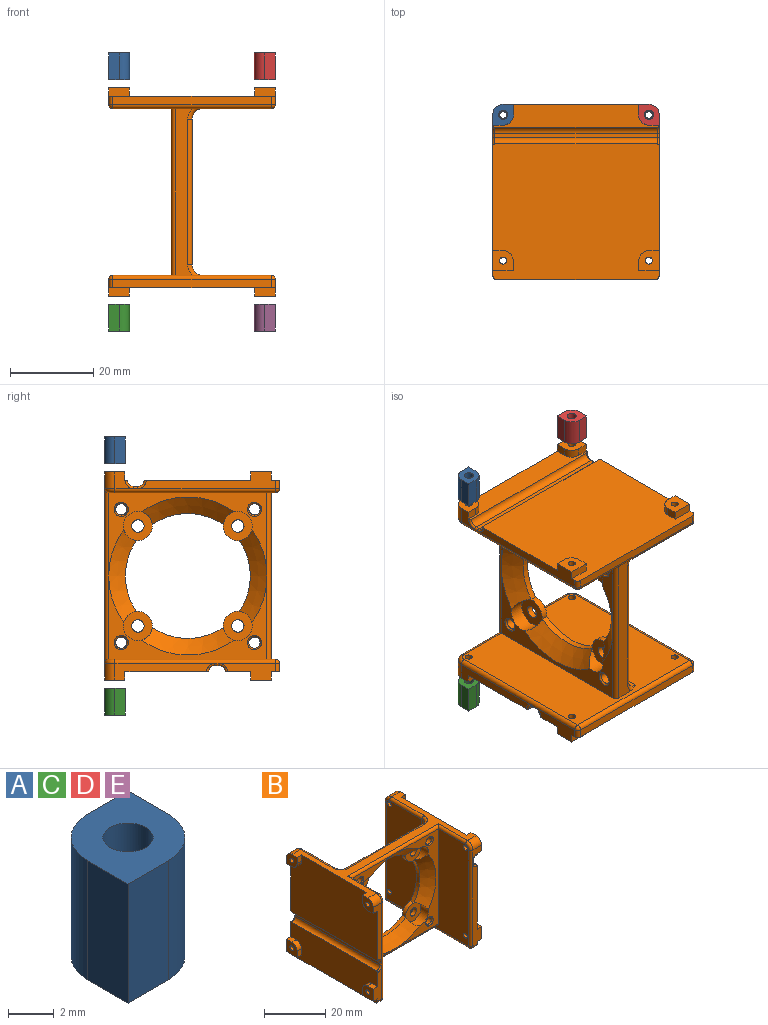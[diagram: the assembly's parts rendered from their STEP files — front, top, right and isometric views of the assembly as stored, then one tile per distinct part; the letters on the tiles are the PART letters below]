
ASSEMBLY  parts=5 mates=4
PART A: 9 faces, bbox 5x5x6.4 mm
  f0: plane 6.4x2.5mm, normal (1,0,0), area 16mm2, adj f1,f5,f6,f7
  f1: plane 6.4x2.5mm, normal (0,1,0), area 16mm2, adj f0,f2,f6,f7
  f2: cylinder r=2.5mm len=6.4mm, axis (0,0,-1), area 25.1mm2, adj f1,f3,f6,f7
  f3: plane 6.4x2.5mm, normal (-1,0,0), area 16mm2, adj f2,f4,f6,f7
  f4: plane 6.4x2.5mm, normal (0,-1,0), area 16mm2, adj f3,f5,f6,f7
  f5: cylinder r=2.5mm len=6.4mm, axis (0,0,-1), area 25.1mm2, adj f0,f4,f6,f7
  f6: plane 5x5mm, normal (0,0,1), area 18.5mm2, adj f0,f1,f2,f3,f4,f5,f8
  f7: plane 5x5mm, normal (0,0,-1), area 18.5mm2, adj f0,f1,f2,f3,f4,f5,f8
  f8: cylinder r=1.1mm len=6.4mm, axis (0,0,-1), area 44.2mm2, adj f6,f7
PART B: 151 faces, bbox 50x40.4x42.2 mm
  f0: plane 13.5x4mm, normal (0,-1,0), area 33.7mm2, adj f5,f10,f63,f66,f122,f126,f150
  f1: plane 13.5x4mm, normal (0,1,0), area 33.7mm2, adj f6,f10,f61,f62,f115,f116,f147
  f2: plane 33x4mm, normal (0,-1,0), area 72.7mm2, adj f8,f16,f78,f79,f117,f123,f144
  f3: plane 33x4mm, normal (0,1,0), area 72.7mm2, adj f7,f16,f80,f83,f111,f112,f141
  f4: plane 38x20mm, normal (0,-1,0), area 162.1mm2, adj f14,f19,f23,f29,f35,f41,f44,f50
  f5: plane 4.9x2mm, normal (0,0,-1), area 9.8mm2, adj f0,f10,f65,f66
  f6: plane 4.9x2mm, normal (0,0,-1), area 9.8mm2, adj f1,f10,f59,f62
  f7: plane 4.9x2mm, normal (0,0,-1), area 9.8mm2, adj f3,f16,f82,f83
  f8: plane 4.9x2mm, normal (0,0,-1), area 9.8mm2, adj f2,f16,f76,f79
  f9: plane 40x5.5mm, normal (1,0,0), area 174.3mm2, adj f12,f15,f26,f72,f73,f74,f85,f86
  f10: plane 40x13mm, normal (-1,0,0), area 473.9mm2, adj f0,f1,f5,f6,f59,f60,f61,f63
  f11: plane 24x4mm, normal (0,1,0), area 49.7mm2, adj f17,f56,f58,f97,f115,f145
  f12: plane 4.5x4mm, normal (0,1,0), area 10.7mm2, adj f9,f84,f87,f88,f112,f139
  f13: plane 40x38mm, normal (-1,0,0), area 1218.6mm2, adj f18,f28,f89,f90,f91,f92,f103,f107
  f14: plane 40x38mm, normal (1,0,0), area 1218.6mm2, adj f4,f28,f93,f94,f95,f96,f104,f110
  f15: plane 50x35mm, normal (0,0,1), area 290.5mm2, adj f9,f17,f55,f58,f67,f70,f71,f74
  f16: plane 40x32.5mm, normal (1,0,0), area 1253.9mm2, adj f2,f3,f7,f8,f76,f77,f78,f80
  f17: plane 40x25mm, normal (-1,0,0), area 954.3mm2, adj f11,f15,f25,f55,f56,f57,f67,f68
  f18: plane 38x20mm, normal (0,-1,0), area 162.1mm2, adj f13,f19,f21,f23,f37,f39,f46,f48
  f19: cone r=19mm half-angle=48.8deg, axis (0,-1,0), area 106.8mm2, adj f4,f18,f20,f35,f37
  f20: cylinder r=15mm len=17.03mm, axis (0,-1,0), area 27.2mm2, adj f19,f27,f33,f34
  f21: cone r=19mm half-angle=48.8deg, axis (0,-1,0), area 106.8mm2, adj f18,f22,f37,f39
  f22: cylinder r=15mm len=17.03mm, axis (0,-1,0), area 27.2mm2, adj f21,f27,f32,f33
  f23: cone r=19mm half-angle=48.8deg, axis (0,-1,0), area 106.8mm2, adj f4,f18,f24,f39,f41
  f24: cylinder r=15mm len=17.03mm, axis (0,-1,0), area 27.2mm2, adj f23,f27,f31,f32
  f25: plane 24x4mm, normal (0,-1,0), area 49.7mm2, adj f17,f69,f70,f98,f126,f148
  f26: plane 4.5x4mm, normal (0,-1,0), area 10.7mm2, adj f9,f71,f72,f75,f123,f142
  f27: plane 38x35mm, normal (0,1,0), area 594.9mm2, adj f20,f22,f24,f30,f31,f32,f33,f34
  f28: plane 40x4.05mm, normal (0,0,-1), area 121.6mm2, adj f13,f14,f131,f132,f133,f134
  f29: cone r=19mm half-angle=48.8deg, axis (0,-1,0), area 106.8mm2, adj f4,f30,f35,f41
  f30: cylinder r=15mm len=17.03mm, axis (0,-1,0), area 27.2mm2, adj f27,f29,f31,f34
  f31: cylinder r=3.5mm len=3.85mm, axis (0,-1,0), area 9.3mm2, adj f24,f27,f30,f42
  f32: cylinder r=3.5mm len=3.85mm, axis (0,-1,0), area 9.3mm2, adj f22,f24,f27,f40
  f33: cylinder r=3.5mm len=3.85mm, axis (0,-1,0), area 9.3mm2, adj f20,f22,f27,f38
  f34: cylinder r=3.5mm len=3.85mm, axis (0,-1,0), area 9.3mm2, adj f20,f27,f30,f36
  f35: cylinder r=3.5mm len=6.98mm, axis (0,-1,0), area 40.3mm2, adj f4,f19,f29,f36
  f36: plane 7x7mm, normal (0,-1,0), area 31.4mm2, adj f34,f35,f54
  f37: cylinder r=3.5mm len=6.98mm, axis (0,-1,0), area 40.3mm2, adj f18,f19,f21,f38
  f38: plane 7x7mm, normal (0,-1,0), area 31.4mm2, adj f33,f37,f53
  f39: cylinder r=3.5mm len=6.98mm, axis (0,-1,0), area 40.3mm2, adj f18,f21,f23,f40
  f40: plane 7x7mm, normal (0,-1,0), area 31.4mm2, adj f32,f39,f52
  f41: cylinder r=3.5mm len=6.98mm, axis (0,-1,0), area 40.3mm2, adj f4,f23,f29,f42
  f42: plane 7x7mm, normal (0,-1,0), area 31.4mm2, adj f31,f41,f51
  f43: cylinder r=1.35mm len=4.58mm, axis (0,-1,0), area 38.9mm2, adj f27,f44
  f44: cone r=1.35mm half-angle=40deg, axis (0,-1,0), area 5.2mm2, adj f4,f43
  f45: cylinder r=1.35mm len=4.58mm, axis (0,-1,0), area 38.9mm2, adj f27,f46
  f46: cone r=1.35mm half-angle=40deg, axis (0,-1,0), area 5.2mm2, adj f18,f45
  f47: cylinder r=1.35mm len=4.58mm, axis (0,-1,0), area 38.9mm2, adj f27,f48
  f48: cone r=1.35mm half-angle=40deg, axis (0,-1,0), area 5.2mm2, adj f18,f47
  f49: cylinder r=1.35mm len=4.58mm, axis (0,-1,0), area 38.9mm2, adj f27,f50
  f50: cone r=1.35mm half-angle=40deg, axis (0,-1,0), area 5.2mm2, adj f4,f49
  f51: cylinder r=1.5mm len=3mm, axis (0,-1,0), area 14.1mm2, adj f27,f42
  f52: cylinder r=1.5mm len=3mm, axis (0,-1,0), area 14.1mm2, adj f27,f40
  f53: cylinder r=1.5mm len=3mm, axis (0,-1,0), area 14.1mm2, adj f27,f38
  f54: cylinder r=1.5mm len=3mm, axis (0,-1,0), area 14.1mm2, adj f27,f36
  f55: plane 2.5x2mm, normal (0,-1,0), area 5mm2, adj f15,f17,f57,f58
  f56: plane 2.5x2mm, normal (0,0,-1), area 5mm2, adj f11,f17,f57,f58
  f57: cylinder r=2.4mm len=2.4mm, axis (1,0,0), area 7.5mm2, adj f17,f55,f56,f58
  f58: plane 4.9x4.9mm, normal (-1,0,0), area 19.2mm2, adj f11,f15,f55,f56,f57,f96,f97
  f59: plane 2.5x2mm, normal (0,-1,0), area 5mm2, adj f6,f10,f60,f62
  f60: cylinder r=2.4mm len=2.4mm, axis (1,0,0), area 7.5mm2, adj f10,f59,f61,f62
  f61: plane 2.5x2mm, normal (0,0,1), area 5mm2, adj f1,f10,f60,f62
  f62: plane 4.9x4.9mm, normal (-1,0,0), area 20.5mm2, adj f1,f6,f59,f60,f61,f95
  f63: plane 2.5x2mm, normal (0,0,1), area 5mm2, adj f0,f10,f64,f66
  f64: cylinder r=2.4mm len=2.4mm, axis (1,0,0), area 7.5mm2, adj f10,f63,f65,f66
  f65: plane 2.5x2mm, normal (0,1,0), area 5mm2, adj f5,f10,f64,f66
  f66: plane 4.9x4.9mm, normal (-1,0,0), area 20.5mm2, adj f0,f5,f63,f64,f65,f94
  f67: plane 2.5x2mm, normal (0,1,0), area 5mm2, adj f15,f17,f68,f70
  f68: cylinder r=2.4mm len=2.4mm, axis (1,0,0), area 7.5mm2, adj f17,f67,f69,f70
  f69: plane 2.5x2mm, normal (0,0,-1), area 5mm2, adj f17,f25,f68,f70
  f70: plane 4.9x4.9mm, normal (-1,0,0), area 19.2mm2, adj f15,f25,f67,f68,f69,f93,f98
  f71: cylinder r=2.5mm len=4mm, axis (-1,0,0), area 15.7mm2, adj f15,f26,f75,f125
  f72: plane 2.5x2mm, normal (0,0,-1), area 5mm2, adj f9,f26,f73,f75
  f73: cylinder r=2.4mm len=2.4mm, axis (-1,0,0), area 7.5mm2, adj f9,f72,f74,f75
  f74: plane 2.5x2mm, normal (0,1,0), area 5mm2, adj f9,f15,f73,f75
  f75: plane 4.9x4.9mm, normal (1,0,0), area 19.2mm2, adj f15,f26,f71,f72,f73,f74,f92
  f76: plane 2.5x2mm, normal (0,1,0), area 5mm2, adj f8,f16,f77,f79
  f77: cylinder r=2.4mm len=2.4mm, axis (-1,0,0), area 7.5mm2, adj f16,f76,f78,f79
  f78: plane 2.5x2mm, normal (0,0,1), area 5mm2, adj f2,f16,f77,f79
  f79: plane 4.9x4.9mm, normal (1,0,0), area 20.5mm2, adj f2,f8,f76,f77,f78,f91
  f80: plane 2.5x2mm, normal (0,0,1), area 5mm2, adj f3,f16,f81,f83
  f81: cylinder r=2.4mm len=2.4mm, axis (-1,0,0), area 7.5mm2, adj f16,f80,f82,f83
  f82: plane 2.5x2mm, normal (0,-1,0), area 5mm2, adj f7,f16,f81,f83
  f83: plane 4.9x4.9mm, normal (1,0,0), area 20.5mm2, adj f3,f7,f80,f81,f82,f90
  f84: cylinder r=2.5mm len=4mm, axis (-1,0,0), area 15.7mm2, adj f12,f15,f88,f109
  f85: plane 2.5x2mm, normal (0,-1,0), area 5mm2, adj f9,f15,f86,f88
  f86: cylinder r=2.4mm len=2.4mm, axis (-1,0,0), area 7.5mm2, adj f9,f85,f87,f88
  f87: plane 2.5x2mm, normal (0,0,-1), area 5mm2, adj f9,f12,f86,f88
  f88: plane 4.9x4.9mm, normal (1,0,0), area 19.2mm2, adj f12,f15,f84,f85,f86,f87,f89
  f89: cylinder r=0.85mm len=5mm, axis (-1,0,0), area 26.7mm2, adj f13,f88
  f90: cylinder r=0.85mm len=5mm, axis (-1,0,0), area 26.7mm2, adj f13,f83
  f91: cylinder r=0.85mm len=5mm, axis (-1,0,0), area 26.7mm2, adj f13,f79
  f92: cylinder r=0.85mm len=5mm, axis (-1,0,0), area 26.7mm2, adj f13,f75
  f93: cylinder r=0.85mm len=5mm, axis (-1,0,0), area 26.7mm2, adj f14,f70
  f94: cylinder r=0.85mm len=5mm, axis (-1,0,0), area 26.7mm2, adj f14,f66
  f95: cylinder r=0.85mm len=5mm, axis (-1,0,0), area 26.7mm2, adj f14,f62
  f96: cylinder r=0.85mm len=5mm, axis (-1,0,0), area 26.7mm2, adj f14,f58
  f97: cylinder r=2.5mm len=4mm, axis (-1,0,0), area 15.7mm2, adj f11,f15,f58,f113
  f98: cylinder r=2.5mm len=4mm, axis (-1,0,0), area 15.7mm2, adj f15,f25,f70,f128
  f99: plane 39x1mm, normal (1,0,0), area 39mm2, adj f137,f138,f140,f143
  f100: plane 39x1mm, normal (-1,0,0), area 39mm2, adj f135,f136,f146,f149
  f101: plane 38x2mm, normal (0,0,-1), area 76mm2, adj f16,f111,f117,f118
  f102: plane 38x2mm, normal (0,0,-1), area 76mm2, adj f10,f116,f121,f122
  f103: cylinder r=2.5mm len=38mm, axis (0,0,1), area 149.2mm2, adj f13,f27,f105,f133
  f104: cylinder r=2.5mm len=38mm, axis (0,0,1), area 149.2mm2, adj f14,f27,f108,f131
  f105: torus R=3.5mm, axis (0,0,1), area 7.1mm2, adj f15,f103,f106,f107
  f106: cylinder r=1mm len=35mm, axis (1,0,0), area 55mm2, adj f15,f27,f105,f108
  f107: cylinder r=1mm len=15mm, axis (0,1,0), area 23.6mm2, adj f13,f15,f105,f109
  f108: torus R=3.5mm, axis (0,0,1), area 7.1mm2, adj f15,f104,f106,f110
  f109: torus R=1.5mm, axis (1,0,0), area 5.3mm2, adj f13,f84,f107,f112
  f110: cylinder r=1mm len=15mm, axis (0,-1,0), area 23.6mm2, adj f14,f15,f108,f113
  f111: cylinder r=1mm len=2mm, axis (1,0,0), area 3.1mm2, adj f3,f16,f101,f114
  f112: cylinder r=1mm len=38.5mm, axis (0,0,-1), area 60.5mm2, adj f3,f12,f13,f109,f114,f140
  f113: torus R=1.5mm, axis (-1,0,0), area 5.3mm2, adj f14,f97,f110,f115
  f114: sphere r=1mm, area 1.6mm2, adj f111,f112,f118
  f115: cylinder r=1mm len=38.5mm, axis (0,0,-1), area 60.5mm2, adj f1,f11,f14,f113,f119,f146
  f116: cylinder r=1mm len=2mm, axis (1,0,0), area 3.1mm2, adj f1,f10,f102,f119
  f117: cylinder r=1mm len=2mm, axis (-1,0,0), area 3.1mm2, adj f2,f16,f101,f120
  f118: cylinder r=1mm len=38mm, axis (0,1,0), area 59.7mm2, adj f13,f101,f114,f120
  f119: sphere r=1mm, area 1.6mm2, adj f115,f116,f121
  f120: sphere r=1mm, area 1.6mm2, adj f117,f118,f123
  f121: cylinder r=1mm len=38mm, axis (0,-1,0), area 59.7mm2, adj f14,f102,f119,f124
  f122: cylinder r=1mm len=2mm, axis (-1,0,0), area 3.1mm2, adj f0,f10,f102,f124
  f123: cylinder r=1mm len=38.5mm, axis (0,0,-1), area 60.5mm2, adj f2,f13,f26,f120,f125,f143
  f124: sphere r=1mm, area 1.6mm2, adj f121,f122,f126
  f125: torus R=1.5mm, axis (1,0,0), area 5.3mm2, adj f13,f71,f123,f127
  f126: cylinder r=1mm len=38.5mm, axis (0,0,-1), area 60.5mm2, adj f0,f14,f25,f124,f128,f149
  f127: cylinder r=1mm len=13.5mm, axis (0,1,0), area 20.2mm2, adj f13,f15,f125,f129
  f128: torus R=1.5mm, axis (-1,0,0), area 5.3mm2, adj f14,f98,f126,f130
  f129: cylinder r=1mm len=42mm, axis (-1,0,0), area 64mm2, adj f4,f15,f18,f127,f130
  f130: cylinder r=1mm len=13.5mm, axis (0,-1,0), area 20.2mm2, adj f14,f15,f128,f129
  f131: torus R=3.5mm, axis (0,0,1), area 5mm2, adj f14,f28,f104,f132
  f132: cylinder r=1mm len=35mm, axis (-1,0,0), area 55mm2, adj f27,f28,f131,f133
  f133: torus R=3.5mm, axis (0,0,1), area 5mm2, adj f13,f28,f103,f132
  f134: cylinder r=1mm len=40mm, axis (1,0,0), area 62.8mm2, adj f4,f13,f14,f18,f28
  f135: cylinder r=1.5mm len=39mm, axis (0,1,0), area 91.9mm2, adj f10,f100,f147,f150
  f136: cylinder r=1.5mm len=39mm, axis (0,1,0), area 91.9mm2, adj f17,f100,f145,f148
  f137: cylinder r=1.5mm len=39mm, axis (0,1,0), area 91.9mm2, adj f9,f99,f139,f142
  f138: cylinder r=1.5mm len=39mm, axis (0,1,0), area 91.9mm2, adj f16,f99,f141,f144
  f139: torus R=2mm, axis (0,-1,0), area 2.1mm2, adj f9,f12,f137,f140
  f140: cylinder r=0.5mm len=1mm, axis (0,0,-1), area 0.8mm2, adj f99,f112,f139,f141
  f141: torus R=2mm, axis (0,-1,0), area 2.1mm2, adj f3,f16,f138,f140
  f142: torus R=2mm, axis (0,1,0), area 2.1mm2, adj f9,f26,f137,f143
  f143: cylinder r=0.5mm len=1mm, axis (0,0,-1), area 0.8mm2, adj f99,f123,f142,f144
  f144: torus R=2mm, axis (0,1,0), area 2.1mm2, adj f2,f16,f138,f143
  f145: torus R=2mm, axis (0,-1,0), area 2.1mm2, adj f11,f17,f136,f146
  f146: cylinder r=0.5mm len=1mm, axis (0,0,1), area 0.8mm2, adj f100,f115,f145,f147
  f147: torus R=2mm, axis (0,-1,0), area 2.1mm2, adj f1,f10,f135,f146
  f148: torus R=2mm, axis (0,1,0), area 2.1mm2, adj f17,f25,f136,f149
  f149: cylinder r=0.5mm len=1mm, axis (0,0,1), area 0.8mm2, adj f100,f126,f148,f150
  f150: torus R=2mm, axis (0,1,0), area 2.1mm2, adj f0,f10,f135,f149
PART C: same geometry as A
PART D: same geometry as A
PART E: same geometry as A
PLACE A rot(axis=(0,0,1),180deg) t=(22.31,74.51,78.31)mm
PLACE B rot(axis=(-0.58,-0.58,-0.58),120deg) t=(-10.81,-24.81,79.79)mm
PLACE C t=(-20.17,-49.12,17.91)mm
PLACE D rot(axis=(1,0,0),180deg) t=(14.83,74.51,84.71)mm
PLACE E rot(axis=(1,0,0),180deg) t=(14.83,74.51,24.31)mm
MATE fastened B.f125 <-> C.f2  axis (0,0,-1) through (1.07,12.69,24.31)mm
MATE fastened B.f109 <-> E.f2  axis (0,0,-1) through (36.07,12.69,24.31)mm
MATE fastened A.f2 <-> B.f68  axis (0,0,-1) through (1.07,12.69,78.31)mm
MATE fastened B.f57 <-> D.f2  axis (0,0,1) through (36.07,12.69,78.31)mm
